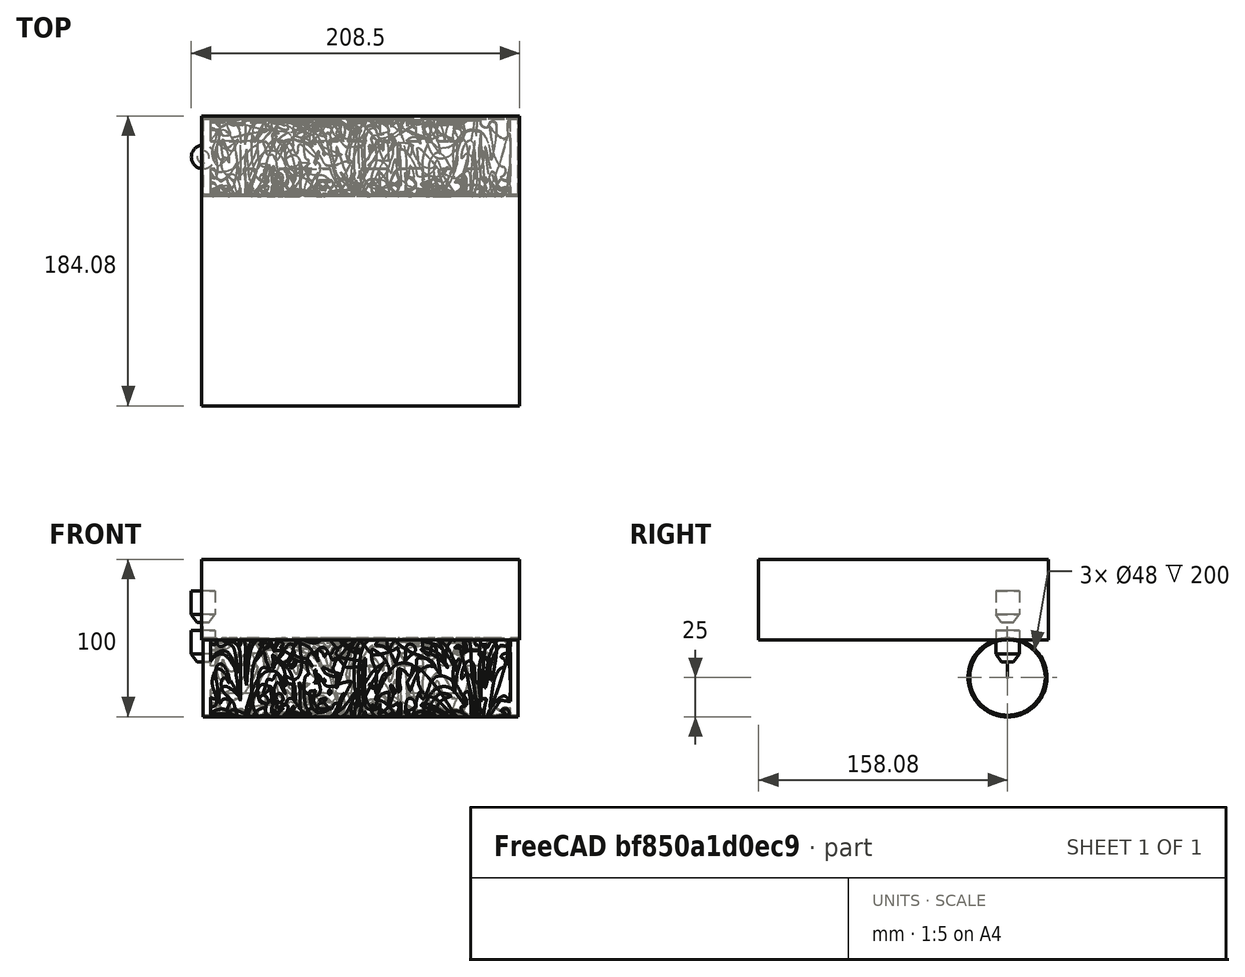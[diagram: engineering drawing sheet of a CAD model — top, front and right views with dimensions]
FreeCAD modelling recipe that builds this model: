
FCSTD DOCUMENT  (FreeCAD 0.20R25747 (Git))
Label: bamboo1
License: All rights reserved
LicenseURL: http://en.wikipedia.org/wiki/All_rights_reserved
objects: Part::FeaturePython×6, Path::FeaturePython×4, Sketcher::SketchObject×2, Part::Feature×2, App::DocumentObjectGroup×2, PartDesign::Pad×1, PartDesign::Body×1, Part::Cut×1, App::Link×1, App::FeaturePython×1, Path::FeatureCompoundPython×1
note: 14 computed .brp shape members not serialized (recipe doc carries the construction recipe); baked Part::Feature solids carry a one-line shape summary decoded from their .brp

FEATURE [Sketcher::SketchObject] Sketch
  FullyConstrained = true
  MapMode = 5
  Placement = pos=(0,0,0) rot=(0.57735,0.57735,0.57735;2.0944rad)
  Support = -> [YZ_Plane]
  sketch-geometry (2):
    g0: Circle CenterX=0 CenterY=0 CenterZ=0 NormalX=0 NormalY=0 NormalZ=1 AngleXU=0 Radius=25
    g1: Circle CenterX=0 CenterY=0 CenterZ=0 NormalX=0 NormalY=0 NormalZ=1 AngleXU=0 Radius=24
  constraints (4):
    c: Coincident(g0,g-1)
    c: Coincident(g1,g0)
    c: Diameter(g0) = 50
    c: Diameter(g1) = 48
FEATURE [PartDesign::Pad] Pad
  Direction = (1,-2e-16,3e-16)
  Length = 200
  Length2 = 100
  Placement = pos=(0,0,0) rot=(0.57735,0.57735,0.57735;2.0944rad)
  Profile = -> Sketch
  Type = 0
FEATURE [PartDesign::Body] Body
  Group = -> [Sketch,Pad]
  Origin = -> Origin
  Tip = -> Pad
FEATURE [Sketcher::SketchObject] Sketch001
  FullyConstrained = false
  Placement = pos=(100,-2.5e-14,5.5e-14) rot=(0.57735,0.57735,0.57735;2.0944rad)
  Support = -> [Pad]
  sketch-geometry (667):
    g0: BSplineCurve PolesCount=4 KnotsCount=2 Degree=3 IsPeriodic=0
    g1: BSplineCurve PolesCount=2 KnotsCount=2 Degree=1 IsPeriodic=0
    g2: BSplineCurve PolesCount=2 KnotsCount=2 Degree=1 IsPeriodic=0
    g3: BSplineCurve PolesCount=4 KnotsCount=2 Degree=3 IsPeriodic=0
    g4: BSplineCurve PolesCount=4 KnotsCount=2 Degree=3 IsPeriodic=0
    g5: BSplineCurve PolesCount=4 KnotsCount=2 Degree=3 IsPeriodic=0
    g6: BSplineCurve PolesCount=3 KnotsCount=2 Degree=2 IsPeriodic=0
    g7: BSplineCurve PolesCount=4 KnotsCount=2 Degree=3 IsPeriodic=0
    g8: BSplineCurve PolesCount=4 KnotsCount=2 Degree=3 IsPeriodic=0
    g9: BSplineCurve PolesCount=4 KnotsCount=2 Degree=3 IsPeriodic=0
    g10: BSplineCurve PolesCount=2 KnotsCount=2 Degree=1 IsPeriodic=0
    g11: BSplineCurve PolesCount=2 KnotsCount=2 Degree=1 IsPeriodic=0
    g12: BSplineCurve PolesCount=4 KnotsCount=2 Degree=3 IsPeriodic=0
    g13: BSplineCurve PolesCount=4 KnotsCount=2 Degree=3 IsPeriodic=0
    g14: BSplineCurve PolesCount=4 KnotsCount=2 Degree=3 IsPeriodic=0
    g15: BSplineCurve PolesCount=4 KnotsCount=2 Degree=3 IsPeriodic=0
    g16: BSplineCurve PolesCount=4 KnotsCount=2 Degree=3 IsPeriodic=0
    g17: BSplineCurve PolesCount=4 KnotsCount=2 Degree=3 IsPeriodic=0
    g18: BSplineCurve PolesCount=4 KnotsCount=2 Degree=3 IsPeriodic=0
    g19: BSplineCurve PolesCount=4 KnotsCount=2 Degree=3 IsPeriodic=0
    g20: BSplineCurve PolesCount=4 KnotsCount=2 Degree=3 IsPeriodic=0
    g21: BSplineCurve PolesCount=4 KnotsCount=2 Degree=3 IsPeriodic=0
    g22: BSplineCurve PolesCount=4 KnotsCount=2 Degree=3 IsPeriodic=0
    g23: BSplineCurve PolesCount=4 KnotsCount=2 Degree=3 IsPeriodic=0
    g24: BSplineCurve PolesCount=4 KnotsCount=2 Degree=3 IsPeriodic=0
    g25: BSplineCurve PolesCount=4 KnotsCount=2 Degree=3 IsPeriodic=0
    g26: BSplineCurve PolesCount=4 KnotsCount=2 Degree=3 IsPeriodic=0
    g27: BSplineCurve PolesCount=4 KnotsCount=2 Degree=3 IsPeriodic=0
    g28: BSplineCurve PolesCount=4 KnotsCount=2 Degree=3 IsPeriodic=0
    g29: BSplineCurve PolesCount=4 KnotsCount=2 Degree=3 IsPeriodic=0
    g30: BSplineCurve PolesCount=4 KnotsCount=2 Degree=3 IsPeriodic=0
    g31: BSplineCurve PolesCount=4 KnotsCount=2 Degree=3 IsPeriodic=0
    g32: BSplineCurve PolesCount=4 KnotsCount=2 Degree=3 IsPeriodic=0
    g33: BSplineCurve PolesCount=4 KnotsCount=2 Degree=3 IsPeriodic=0
    g34: BSplineCurve PolesCount=2 KnotsCount=2 Degree=1 IsPeriodic=0
    g35: BSplineCurve PolesCount=2 KnotsCount=2 Degree=1 IsPeriodic=0
    g36: BSplineCurve PolesCount=4 KnotsCount=2 Degree=3 IsPeriodic=0
    g37: BSplineCurve PolesCount=4 KnotsCount=2 Degree=3 IsPeriodic=0
    g38: BSplineCurve PolesCount=2 KnotsCount=2 Degree=1 IsPeriodic=0
    g39: BSplineCurve PolesCount=2 KnotsCount=2 Degree=1 IsPeriodic=0
    g40: BSplineCurve PolesCount=4 KnotsCount=2 Degree=3 IsPeriodic=0
    g41: BSplineCurve PolesCount=4 KnotsCount=2 Degree=3 IsPeriodic=0
    g42: BSplineCurve PolesCount=4 KnotsCount=2 Degree=3 IsPeriodic=0
    g43: BSplineCurve PolesCount=4 KnotsCount=2 Degree=3 IsPeriodic=0
    g44: BSplineCurve PolesCount=3 KnotsCount=2 Degree=2 IsPeriodic=0
    g45: BSplineCurve PolesCount=4 KnotsCount=2 Degree=3 IsPeriodic=0
    g46: BSplineCurve PolesCount=4 KnotsCount=2 Degree=3 IsPeriodic=0
    g47: BSplineCurve PolesCount=2 KnotsCount=2 Degree=1 IsPeriodic=0
    g48: BSplineCurve PolesCount=2 KnotsCount=2 Degree=1 IsPeriodic=0
    g49: BSplineCurve PolesCount=4 KnotsCount=2 Degree=3 IsPeriodic=0
    g50: BSplineCurve PolesCount=4 KnotsCount=2 Degree=3 IsPeriodic=0
    g51: BSplineCurve PolesCount=4 KnotsCount=2 Degree=3 IsPeriodic=0
    g52: BSplineCurve PolesCount=4 KnotsCount=2 Degree=3 IsPeriodic=0
    g53: BSplineCurve PolesCount=4 KnotsCount=2 Degree=3 IsPeriodic=0
    g54: BSplineCurve PolesCount=4 KnotsCount=2 Degree=3 IsPeriodic=0
    g55: BSplineCurve PolesCount=4 KnotsCount=2 Degree=3 IsPeriodic=0
    g56: BSplineCurve PolesCount=4 KnotsCount=2 Degree=3 IsPeriodic=0
    g57: BSplineCurve PolesCount=4 KnotsCount=2 Degree=3 IsPeriodic=0
    g58: BSplineCurve PolesCount=4 KnotsCount=2 Degree=3 IsPeriodic=0
    g59: BSplineCurve PolesCount=4 KnotsCount=2 Degree=3 IsPeriodic=0
    g60: BSplineCurve PolesCount=4 KnotsCount=2 Degree=3 IsPeriodic=0
    g61: BSplineCurve PolesCount=4 KnotsCount=2 Degree=3 IsPeriodic=0
    g62: BSplineCurve PolesCount=2 KnotsCount=2 Degree=1 IsPeriodic=0
    g63: BSplineCurve PolesCount=2 KnotsCount=2 Degree=1 IsPeriodic=0
    g64: BSplineCurve PolesCount=4 KnotsCount=2 Degree=3 IsPeriodic=0
    g65: BSplineCurve PolesCount=4 KnotsCount=2 Degree=3 IsPeriodic=0
    g66: BSplineCurve PolesCount=2 KnotsCount=2 Degree=1 IsPeriodic=0
    g67: BSplineCurve PolesCount=4 KnotsCount=2 Degree=3 IsPeriodic=0
    g68: BSplineCurve PolesCount=4 KnotsCount=2 Degree=3 IsPeriodic=0
    g69: BSplineCurve PolesCount=4 KnotsCount=2 Degree=3 IsPeriodic=0
    g70: BSplineCurve PolesCount=4 KnotsCount=2 Degree=3 IsPeriodic=0
    g71: BSplineCurve PolesCount=4 KnotsCount=2 Degree=3 IsPeriodic=0
    g72: BSplineCurve PolesCount=4 KnotsCount=2 Degree=3 IsPeriodic=0
    g73: BSplineCurve PolesCount=4 KnotsCount=2 Degree=3 IsPeriodic=0
    g74: BSplineCurve PolesCount=4 KnotsCount=2 Degree=3 IsPeriodic=0
    g75: BSplineCurve PolesCount=4 KnotsCount=2 Degree=3 IsPeriodic=0
    g76: BSplineCurve PolesCount=4 KnotsCount=2 Degree=3 IsPeriodic=0
    g77: BSplineCurve PolesCount=4 KnotsCount=2 Degree=3 IsPeriodic=0
    g78: BSplineCurve PolesCount=4 KnotsCount=2 Degree=3 IsPeriodic=0
    g79: BSplineCurve PolesCount=4 KnotsCount=2 Degree=3 IsPeriodic=0
    g80: BSplineCurve PolesCount=4 KnotsCount=2 Degree=3 IsPeriodic=0
    g81: BSplineCurve PolesCount=4 KnotsCount=2 Degree=3 IsPeriodic=0
    g82: BSplineCurve PolesCount=4 KnotsCount=2 Degree=3 IsPeriodic=0
    g83: BSplineCurve PolesCount=4 KnotsCount=2 Degree=3 IsPeriodic=0
    g84: BSplineCurve PolesCount=4 KnotsCount=2 Degree=3 IsPeriodic=0
    g85: BSplineCurve PolesCount=4 KnotsCount=2 Degree=3 IsPeriodic=0
    g86: BSplineCurve PolesCount=4 KnotsCount=2 Degree=3 IsPeriodic=0
    g87: BSplineCurve PolesCount=4 KnotsCount=2 Degree=3 IsPeriodic=0
    g88: BSplineCurve PolesCount=2 KnotsCount=2 Degree=1 IsPeriodic=0
    g89: BSplineCurve PolesCount=2 KnotsCount=2 Degree=1 IsPeriodic=0
    g90: BSplineCurve PolesCount=4 KnotsCount=2 Degree=3 IsPeriodic=0
    g91: BSplineCurve PolesCount=4 KnotsCount=2 Degree=3 IsPeriodic=0
    g92: BSplineCurve PolesCount=4 KnotsCount=2 Degree=3 IsPeriodic=0
    g93: BSplineCurve PolesCount=4 KnotsCount=2 Degree=3 IsPeriodic=0
    g94: BSplineCurve PolesCount=4 KnotsCount=2 Degree=3 IsPeriodic=0
    g95: BSplineCurve PolesCount=4 KnotsCount=2 Degree=3 IsPeriodic=0
    g96: BSplineCurve PolesCount=4 KnotsCount=2 Degree=3 IsPeriodic=0
    g97: BSplineCurve PolesCount=4 KnotsCount=2 Degree=3 IsPeriodic=0
    g98: BSplineCurve PolesCount=4 KnotsCount=2 Degree=3 IsPeriodic=0
    g99: BSplineCurve PolesCount=4 KnotsCount=2 Degree=3 IsPeriodic=0
    g100: BSplineCurve PolesCount=4 KnotsCount=2 Degree=3 IsPeriodic=0
    g101: BSplineCurve PolesCount=4 KnotsCount=2 Degree=3 IsPeriodic=0
    g102: BSplineCurve PolesCount=4 KnotsCount=2 Degree=3 IsPeriodic=0
    g103: BSplineCurve PolesCount=2 KnotsCount=2 Degree=1 IsPeriodic=0
    g104: BSplineCurve PolesCount=2 KnotsCount=2 Degree=1 IsPeriodic=0
    g105: BSplineCurve PolesCount=4 KnotsCount=2 Degree=3 IsPeriodic=0
    g106: BSplineCurve PolesCount=2 KnotsCount=2 Degree=1 IsPeriodic=0
    g107: BSplineCurve PolesCount=2 KnotsCount=2 Degree=1 IsPeriodic=0
    g108: BSplineCurve PolesCount=2 KnotsCount=2 Degree=1 IsPeriodic=0
    g109: BSplineCurve PolesCount=2 KnotsCount=2 Degree=1 IsPeriodic=0
    g110: BSplineCurve PolesCount=4 KnotsCount=2 Degree=3 IsPeriodic=0
    g111: BSplineCurve PolesCount=4 KnotsCount=2 Degree=3 IsPeriodic=0
    g112: BSplineCurve PolesCount=4 KnotsCount=2 Degree=3 IsPeriodic=0
    g113: BSplineCurve PolesCount=4 KnotsCount=2 Degree=3 IsPeriodic=0
    g114: BSplineCurve PolesCount=4 KnotsCount=2 Degree=3 IsPeriodic=0
    g115: BSplineCurve PolesCount=4 KnotsCount=2 Degree=3 IsPeriodic=0
    g116: BSplineCurve PolesCount=4 KnotsCount=2 Degree=3 IsPeriodic=0
    g117: BSplineCurve PolesCount=4 KnotsCount=2 Degree=3 IsPeriodic=0
    g118: BSplineCurve PolesCount=4 KnotsCount=2 Degree=3 IsPeriodic=0
    g119: BSplineCurve PolesCount=4 KnotsCount=2 Degree=3 IsPeriodic=0
    g120: BSplineCurve PolesCount=4 KnotsCount=2 Degree=3 IsPeriodic=0
    g121: BSplineCurve PolesCount=4 KnotsCount=2 Degree=3 IsPeriodic=0
    g122: BSplineCurve PolesCount=4 KnotsCount=2 Degree=3 IsPeriodic=0
    g123: BSplineCurve PolesCount=4 KnotsCount=2 Degree=3 IsPeriodic=0
    g124: BSplineCurve PolesCount=4 KnotsCount=2 Degree=3 IsPeriodic=0
    g125: BSplineCurve PolesCount=4 KnotsCount=2 Degree=3 IsPeriodic=0
    g126: BSplineCurve PolesCount=4 KnotsCount=2 Degree=3 IsPeriodic=0
    g127: BSplineCurve PolesCount=4 KnotsCount=2 Degree=3 IsPeriodic=0
    g128: BSplineCurve PolesCount=4 KnotsCount=2 Degree=3 IsPeriodic=0
    g129: BSplineCurve PolesCount=4 KnotsCount=2 Degree=3 IsPeriodic=0
    g130: BSplineCurve PolesCount=4 KnotsCount=2 Degree=3 IsPeriodic=0
    g131: BSplineCurve PolesCount=4 KnotsCount=2 Degree=3 IsPeriodic=0
    g132: BSplineCurve PolesCount=4 KnotsCount=2 Degree=3 IsPeriodic=0
    g133: BSplineCurve PolesCount=4 KnotsCount=2 Degree=3 IsPeriodic=0
    g134: BSplineCurve PolesCount=4 KnotsCount=2 Degree=3 IsPeriodic=0
    g135: BSplineCurve PolesCount=4 KnotsCount=2 Degree=3 IsPeriodic=0
    g136: BSplineCurve PolesCount=4 KnotsCount=2 Degree=3 IsPeriodic=0
    g137: BSplineCurve PolesCount=4 KnotsCount=2 Degree=3 IsPeriodic=0
    g138: BSplineCurve PolesCount=4 KnotsCount=2 Degree=3 IsPeriodic=0
    g139: BSplineCurve PolesCount=3 KnotsCount=2 Degree=2 IsPeriodic=0
    g140: BSplineCurve PolesCount=4 KnotsCount=2 Degree=3 IsPeriodic=0
    g141: BSplineCurve PolesCount=4 KnotsCount=2 Degree=3 IsPeriodic=0
    g142: BSplineCurve PolesCount=4 KnotsCount=2 Degree=3 IsPeriodic=0
    g143: BSplineCurve PolesCount=4 KnotsCount=2 Degree=3 IsPeriodic=0
    g144: BSplineCurve PolesCount=4 KnotsCount=2 Degree=3 IsPeriodic=0
    g145: BSplineCurve PolesCount=2 KnotsCount=2 Degree=1 IsPeriodic=0
    g146: BSplineCurve PolesCount=2 KnotsCount=2 Degree=1 IsPeriodic=0
    g147: BSplineCurve PolesCount=4 KnotsCount=2 Degree=3 IsPeriodic=0
    g148: BSplineCurve PolesCount=4 KnotsCount=2 Degree=3 IsPeriodic=0
    g149: BSplineCurve PolesCount=4 KnotsCount=2 Degree=3 IsPeriodic=0
    g150: BSplineCurve PolesCount=4 KnotsCount=2 Degree=3 IsPeriodic=0
    g151: BSplineCurve PolesCount=4 KnotsCount=2 Degree=3 IsPeriodic=0
    g152: BSplineCurve PolesCount=4 KnotsCount=2 Degree=3 IsPeriodic=0
    g153: BSplineCurve PolesCount=4 KnotsCount=2 Degree=3 IsPeriodic=0
    g154: BSplineCurve PolesCount=4 KnotsCount=2 Degree=3 IsPeriodic=0
    g155: BSplineCurve PolesCount=4 KnotsCount=2 Degree=3 IsPeriodic=0
    g156: BSplineCurve PolesCount=4 KnotsCount=2 Degree=3 IsPeriodic=0
    g157: BSplineCurve PolesCount=4 KnotsCount=2 Degree=3 IsPeriodic=0
    g158: BSplineCurve PolesCount=4 KnotsCount=2 Degree=3 IsPeriodic=0
    g159: BSplineCurve PolesCount=2 KnotsCount=2 Degree=1 IsPeriodic=0
    g160: BSplineCurve PolesCount=2 KnotsCount=2 Degree=1 IsPeriodic=0
    g161: BSplineCurve PolesCount=4 KnotsCount=2 Degree=3 IsPeriodic=0
    g162: BSplineCurve PolesCount=4 KnotsCount=2 Degree=3 IsPeriodic=0
    g163: BSplineCurve PolesCount=4 KnotsCount=2 Degree=3 IsPeriodic=0
    g164: BSplineCurve PolesCount=4 KnotsCount=2 Degree=3 IsPeriodic=0
    g165: BSplineCurve PolesCount=4 KnotsCount=2 Degree=3 IsPeriodic=0
    g166: BSplineCurve PolesCount=4 KnotsCount=2 Degree=3 IsPeriodic=0
    g167: BSplineCurve PolesCount=4 KnotsCount=2 Degree=3 IsPeriodic=0
    g168: BSplineCurve PolesCount=4 KnotsCount=2 Degree=3 IsPeriodic=0
    g169: BSplineCurve PolesCount=4 KnotsCount=2 Degree=3 IsPeriodic=0
    g170: BSplineCurve PolesCount=2 KnotsCount=2 Degree=1 IsPeriodic=0
    g171: BSplineCurve PolesCount=2 KnotsCount=2 Degree=1 IsPeriodic=0
    g172: BSplineCurve PolesCount=4 KnotsCount=2 Degree=3 IsPeriodic=0
    g173: BSplineCurve PolesCount=4 KnotsCount=2 Degree=3 IsPeriodic=0
    g174: BSplineCurve PolesCount=4 KnotsCount=2 Degree=3 IsPeriodic=0
    g175: BSplineCurve PolesCount=3 KnotsCount=2 Degree=2 IsPeriodic=0
    g176: BSplineCurve PolesCount=4 KnotsCount=2 Degree=3 IsPeriodic=0
    g177: BSplineCurve PolesCount=4 KnotsCount=2 Degree=3 IsPeriodic=0
    g178: BSplineCurve PolesCount=4 KnotsCount=2 Degree=3 IsPeriodic=0
    g179: BSplineCurve PolesCount=4 KnotsCount=2 Degree=3 IsPeriodic=0
    g180: BSplineCurve PolesCount=3 KnotsCount=2 Degree=2 IsPeriodic=0
    g181: BSplineCurve PolesCount=2 KnotsCount=2 Degree=1 IsPeriodic=0
    g182: BSplineCurve PolesCount=2 KnotsCount=2 Degree=1 IsPeriodic=0
    g183: BSplineCurve PolesCount=4 KnotsCount=2 Degree=3 IsPeriodic=0
    g184: BSplineCurve PolesCount=4 KnotsCount=2 Degree=3 IsPeriodic=0
    g185: BSplineCurve PolesCount=2 KnotsCount=2 Degree=1 IsPeriodic=0
    g186: BSplineCurve PolesCount=2 KnotsCount=2 Degree=1 IsPeriodic=0
    g187: BSplineCurve PolesCount=3 KnotsCount=2 Degree=2 IsPeriodic=0
    g188: BSplineCurve PolesCount=4 KnotsCount=2 Degree=3 IsPeriodic=0
    g189: BSplineCurve PolesCount=4 KnotsCount=2 Degree=3 IsPeriodic=0
    g190: BSplineCurve PolesCount=4 KnotsCount=2 Degree=3 IsPeriodic=0
    g191: BSplineCurve PolesCount=4 KnotsCount=2 Degree=3 IsPeriodic=0
    g192: BSplineCurve PolesCount=4 KnotsCount=2 Degree=3 IsPeriodic=0
    g193: BSplineCurve PolesCount=4 KnotsCount=2 Degree=3 IsPeriodic=0
    g194: BSplineCurve PolesCount=4 KnotsCount=2 Degree=3 IsPeriodic=0
    g195: BSplineCurve PolesCount=4 KnotsCount=2 Degree=3 IsPeriodic=0
    g196: BSplineCurve PolesCount=4 KnotsCount=2 Degree=3 IsPeriodic=0
    g197: BSplineCurve PolesCount=4 KnotsCount=2 Degree=3 IsPeriodic=0
    g198: BSplineCurve PolesCount=4 KnotsCount=2 Degree=3 IsPeriodic=0
    g199: BSplineCurve PolesCount=4 KnotsCount=2 Degree=3 IsPeriodic=0
    g200: BSplineCurve PolesCount=4 KnotsCount=2 Degree=3 IsPeriodic=0
    g201: BSplineCurve PolesCount=4 KnotsCount=2 Degree=3 IsPeriodic=0
    g202: BSplineCurve PolesCount=4 KnotsCount=2 Degree=3 IsPeriodic=0
    g203: BSplineCurve PolesCount=4 KnotsCount=2 Degree=3 IsPeriodic=0
    g204: BSplineCurve PolesCount=3 KnotsCount=2 Degree=2 IsPeriodic=0
    g205: BSplineCurve PolesCount=4 KnotsCount=2 Degree=3 IsPeriodic=0
    g206: BSplineCurve PolesCount=2 KnotsCount=2 Degree=1 IsPeriodic=0
    g207: BSplineCurve PolesCount=2 KnotsCount=2 Degree=1 IsPeriodic=0
    g208: BSplineCurve PolesCount=4 KnotsCount=2 Degree=3 IsPeriodic=0
    g209: BSplineCurve PolesCount=4 KnotsCount=2 Degree=3 IsPeriodic=0
    g210: BSplineCurve PolesCount=4 KnotsCount=2 Degree=3 IsPeriodic=0
    g211: BSplineCurve PolesCount=4 KnotsCount=2 Degree=3 IsPeriodic=0
    g212: BSplineCurve PolesCount=4 KnotsCount=2 Degree=3 IsPeriodic=0
    g213: BSplineCurve PolesCount=3 KnotsCount=2 Degree=2 IsPeriodic=0
    g214: BSplineCurve PolesCount=2 KnotsCount=2 Degree=1 IsPeriodic=0
    g215: BSplineCurve PolesCount=4 KnotsCount=2 Degree=3 IsPeriodic=0
    g216: BSplineCurve PolesCount=2 KnotsCount=2 Degree=1 IsPeriodic=0
    g217: BSplineCurve PolesCount=2 KnotsCount=2 Degree=1 IsPeriodic=0
    g218: BSplineCurve PolesCount=4 KnotsCount=2 Degree=3 IsPeriodic=0
    g219: BSplineCurve PolesCount=4 KnotsCount=2 Degree=3 IsPeriodic=0
    g220: BSplineCurve PolesCount=4 KnotsCount=2 Degree=3 IsPeriodic=0
    g221: BSplineCurve PolesCount=4 KnotsCount=2 Degree=3 IsPeriodic=0
    g222: BSplineCurve PolesCount=4 KnotsCount=2 Degree=3 IsPeriodic=0
    g223: BSplineCurve PolesCount=4 KnotsCount=2 Degree=3 IsPeriodic=0
    g224: BSplineCurve PolesCount=4 KnotsCount=2 Degree=3 IsPeriodic=0
    g225: BSplineCurve PolesCount=4 KnotsCount=2 Degree=3 IsPeriodic=0
    g226: BSplineCurve PolesCount=4 KnotsCount=2 Degree=3 IsPeriodic=0
    g227: BSplineCurve PolesCount=2 KnotsCount=2 Degree=1 IsPeriodic=0
    g228: BSplineCurve PolesCount=2 KnotsCount=2 Degree=1 IsPeriodic=0
    g229: BSplineCurve PolesCount=4 KnotsCount=2 Degree=3 IsPeriodic=0
    g230: BSplineCurve PolesCount=4 KnotsCount=2 Degree=3 IsPeriodic=0
    g231: BSplineCurve PolesCount=4 KnotsCount=2 Degree=3 IsPeriodic=0
    g232: BSplineCurve PolesCount=4 KnotsCount=2 Degree=3 IsPeriodic=0
    g233: BSplineCurve PolesCount=4 KnotsCount=2 Degree=3 IsPeriodic=0
    g234: BSplineCurve PolesCount=4 KnotsCount=2 Degree=3 IsPeriodic=0
    g235: BSplineCurve PolesCount=4 KnotsCount=2 Degree=3 IsPeriodic=0
    g236: BSplineCurve PolesCount=4 KnotsCount=2 Degree=3 IsPeriodic=0
    g237: BSplineCurve PolesCount=4 KnotsCount=2 Degree=3 IsPeriodic=0
    g238: BSplineCurve PolesCount=4 KnotsCount=2 Degree=3 IsPeriodic=0
    g239: BSplineCurve PolesCount=4 KnotsCount=2 Degree=3 IsPeriodic=0
    g240: BSplineCurve PolesCount=2 KnotsCount=2 Degree=1 IsPeriodic=0
    g241: BSplineCurve PolesCount=2 KnotsCount=2 Degree=1 IsPeriodic=0
    g242: BSplineCurve PolesCount=4 KnotsCount=2 Degree=3 IsPeriodic=0
    g243: BSplineCurve PolesCount=4 KnotsCount=2 Degree=3 IsPeriodic=0
    g244: BSplineCurve PolesCount=4 KnotsCount=2 Degree=3 IsPeriodic=0
    g245: BSplineCurve PolesCount=4 KnotsCount=2 Degree=3 IsPeriodic=0
    g246: BSplineCurve PolesCount=4 KnotsCount=2 Degree=3 IsPeriodic=0
    g247: BSplineCurve PolesCount=4 KnotsCount=2 Degree=3 IsPeriodic=0
    g248: BSplineCurve PolesCount=4 KnotsCount=2 Degree=3 IsPeriodic=0
    g249: BSplineCurve PolesCount=4 KnotsCount=2 Degree=3 IsPeriodic=0
    g250: BSplineCurve PolesCount=4 KnotsCount=2 Degree=3 IsPeriodic=0
    g251: BSplineCurve PolesCount=2 KnotsCount=2 Degree=1 IsPeriodic=0
    g252: BSplineCurve PolesCount=4 KnotsCount=2 Degree=3 IsPeriodic=0
    g253: BSplineCurve PolesCount=4 KnotsCount=2 Degree=3 IsPeriodic=0
    g254: BSplineCurve PolesCount=4 KnotsCount=2 Degree=3 IsPeriodic=0
    g255: BSplineCurve PolesCount=4 KnotsCount=2 Degree=3 IsPeriodic=0
    g256: BSplineCurve PolesCount=4 KnotsCount=2 Degree=3 IsPeriodic=0
    g257: BSplineCurve PolesCount=4 KnotsCount=2 Degree=3 IsPeriodic=0
    g258: BSplineCurve PolesCount=4 KnotsCount=2 Degree=3 IsPeriodic=0
    g259: BSplineCurve PolesCount=4 KnotsCount=2 Degree=3 IsPeriodic=0
    g260: BSplineCurve PolesCount=4 KnotsCount=2 Degree=3 IsPeriodic=0
    g261: BSplineCurve PolesCount=4 KnotsCount=2 Degree=3 IsPeriodic=0
    g262: BSplineCurve PolesCount=4 KnotsCount=2 Degree=3 IsPeriodic=0
    g263: BSplineCurve PolesCount=4 KnotsCount=2 Degree=3 IsPeriodic=0
    g264: BSplineCurve PolesCount=4 KnotsCount=2 Degree=3 IsPeriodic=0
    g265: BSplineCurve PolesCount=4 KnotsCount=2 Degree=3 IsPeriodic=0
    g266: BSplineCurve PolesCount=4 KnotsCount=2 Degree=3 IsPeriodic=0
    g267: BSplineCurve PolesCount=4 KnotsCount=2 Degree=3 IsPeriodic=0
    g268: BSplineCurve PolesCount=4 KnotsCount=2 Degree=3 IsPeriodic=0
    g269: BSplineCurve PolesCount=4 KnotsCount=2 Degree=3 IsPeriodic=0
    g270: BSplineCurve PolesCount=4 KnotsCount=2 Degree=3 IsPeriodic=0
    g271: BSplineCurve PolesCount=4 KnotsCount=2 Degree=3 IsPeriodic=0
    g272: BSplineCurve PolesCount=4 KnotsCount=2 Degree=3 IsPeriodic=0
    g273: BSplineCurve PolesCount=4 KnotsCount=2 Degree=3 IsPeriodic=0
    g274: BSplineCurve PolesCount=4 KnotsCount=2 Degree=3 IsPeriodic=0
    g275: BSplineCurve PolesCount=2 KnotsCount=2 Degree=1 IsPeriodic=0
    g276: BSplineCurve PolesCount=2 KnotsCount=2 Degree=1 IsPeriodic=0
    g277: BSplineCurve PolesCount=4 KnotsCount=2 Degree=3 IsPeriodic=0
    g278: BSplineCurve PolesCount=4 KnotsCount=2 Degree=3 IsPeriodic=0
    g279: BSplineCurve PolesCount=2 KnotsCount=2 Degree=1 IsPeriodic=0
    g280: BSplineCurve PolesCount=4 KnotsCount=2 Degree=3 IsPeriodic=0
    g281: BSplineCurve PolesCount=4 KnotsCount=2 Degree=3 IsPeriodic=0
    g282: BSplineCurve PolesCount=4 KnotsCount=2 Degree=3 IsPeriodic=0
    g283: BSplineCurve PolesCount=4 KnotsCount=2 Degree=3 IsPeriodic=0
    g284: BSplineCurve PolesCount=2 KnotsCount=2 Degree=1 IsPeriodic=0
    g285: BSplineCurve PolesCount=2 KnotsCount=2 Degree=1 IsPeriodic=0
    g286: BSplineCurve PolesCount=4 KnotsCount=2 Degree=3 IsPeriodic=0
    g287: BSplineCurve PolesCount=4 KnotsCount=2 Degree=3 IsPeriodic=0
    g288: BSplineCurve PolesCount=4 KnotsCount=2 Degree=3 IsPeriodic=0
    g289: BSplineCurve PolesCount=4 KnotsCount=2 Degree=3 IsPeriodic=0
    g290: BSplineCurve PolesCount=4 KnotsCount=2 Degree=3 IsPeriodic=0
    g291: BSplineCurve PolesCount=4 KnotsCount=2 Degree=3 IsPeriodic=0
    g292: BSplineCurve PolesCount=4 KnotsCount=2 Degree=3 IsPeriodic=0
    g293: BSplineCurve PolesCount=4 KnotsCount=2 Degree=3 IsPeriodic=0
    g294: BSplineCurve PolesCount=2 KnotsCount=2 Degree=1 IsPeriodic=0
    g295: BSplineCurve PolesCount=2 KnotsCount=2 Degree=1 IsPeriodic=0
    g296: BSplineCurve PolesCount=3 KnotsCount=2 Degree=2 IsPeriodic=0
    g297: BSplineCurve PolesCount=4 KnotsCount=2 Degree=3 IsPeriodic=0
    g298: BSplineCurve PolesCount=4 KnotsCount=2 Degree=3 IsPeriodic=0
    g299: BSplineCurve PolesCount=4 KnotsCount=2 Degree=3 IsPeriodic=0
    g300: BSplineCurve PolesCount=3 KnotsCount=2 Degree=2 IsPeriodic=0
    g301: BSplineCurve PolesCount=2 KnotsCount=2 Degree=1 IsPeriodic=0
    g302: BSplineCurve PolesCount=2 KnotsCount=2 Degree=1 IsPeriodic=0
    g303: BSplineCurve PolesCount=4 KnotsCount=2 Degree=3 IsPeriodic=0
    g304: BSplineCurve PolesCount=4 KnotsCount=2 Degree=3 IsPeriodic=0
    g305: BSplineCurve PolesCount=2 KnotsCount=2 Degree=1 IsPeriodic=0
    g306: BSplineCurve PolesCount=2 KnotsCount=2 Degree=1 IsPeriodic=0
    g307: BSplineCurve PolesCount=2 KnotsCount=2 Degree=1 IsPeriodic=0
    g308: BSplineCurve PolesCount=2 KnotsCount=2 Degree=1 IsPeriodic=0
    g309: BSplineCurve PolesCount=4 KnotsCount=2 Degree=3 IsPeriodic=0
    g310: BSplineCurve PolesCount=2 KnotsCount=2 Degree=1 IsPeriodic=0
    g311: BSplineCurve PolesCount=2 KnotsCount=2 Degree=1 IsPeriodic=0
    g312: BSplineCurve PolesCount=4 KnotsCount=2 Degree=3 IsPeriodic=0
    g313: BSplineCurve PolesCount=4 KnotsCount=2 Degree=3 IsPeriodic=0
    g314: BSplineCurve PolesCount=4 KnotsCount=2 Degree=3 IsPeriodic=0
    g315: BSplineCurve PolesCount=4 KnotsCount=2 Degree=3 IsPeriodic=0
    g316: BSplineCurve PolesCount=4 KnotsCount=2 Degree=3 IsPeriodic=0
    g317: BSplineCurve PolesCount=4 KnotsCount=2 Degree=3 IsPeriodic=0
    g318: BSplineCurve PolesCount=4 KnotsCount=2 Degree=3 IsPeriodic=0
    g319: BSplineCurve PolesCount=4 KnotsCount=2 Degree=3 IsPeriodic=0
    g320: BSplineCurve PolesCount=4 KnotsCount=2 Degree=3 IsPeriodic=0
    g321: BSplineCurve PolesCount=4 KnotsCount=2 Degree=3 IsPeriodic=0
    g322: BSplineCurve PolesCount=4 KnotsCount=2 Degree=3 IsPeriodic=0
    g323: BSplineCurve PolesCount=4 KnotsCount=2 Degree=3 IsPeriodic=0
    g324: BSplineCurve PolesCount=4 KnotsCount=2 Degree=3 IsPeriodic=0
    g325: BSplineCurve PolesCount=4 KnotsCount=2 Degree=3 IsPeriodic=0
    g326: BSplineCurve PolesCount=4 KnotsCount=2 Degree=3 IsPeriodic=0
    g327: BSplineCurve PolesCount=4 KnotsCount=2 Degree=3 IsPeriodic=0
    g328: BSplineCurve PolesCount=4 KnotsCount=2 Degree=3 IsPeriodic=0
    g329: BSplineCurve PolesCount=4 KnotsCount=2 Degree=3 IsPeriodic=0
    g330: BSplineCurve PolesCount=4 KnotsCount=2 Degree=3 IsPeriodic=0
    g331: BSplineCurve PolesCount=2 KnotsCount=2 Degree=1 IsPeriodic=0
    g332: BSplineCurve PolesCount=2 KnotsCount=2 Degree=1 IsPeriodic=0
    g333: BSplineCurve PolesCount=4 KnotsCount=2 Degree=3 IsPeriodic=0
    g334: BSplineCurve PolesCount=4 KnotsCount=2 Degree=3 IsPeriodic=0
    g335: BSplineCurve PolesCount=4 KnotsCount=2 Degree=3 IsPeriodic=0
    g336: BSplineCurve PolesCount=2 KnotsCount=2 Degree=1 IsPeriodic=0
    g337: BSplineCurve PolesCount=2 KnotsCount=2 Degree=1 IsPeriodic=0
    g338: BSplineCurve PolesCount=4 KnotsCount=2 Degree=3 IsPeriodic=0
    g339: BSplineCurve PolesCount=2 KnotsCount=2 Degree=1 IsPeriodic=0
    g340: BSplineCurve PolesCount=2 KnotsCount=2 Degree=1 IsPeriodic=0
    g341: BSplineCurve PolesCount=2 KnotsCount=2 Degree=1 IsPeriodic=0
    g342: BSplineCurve PolesCount=2 KnotsCount=2 Degree=1 IsPeriodic=0
    g343: BSplineCurve PolesCount=4 KnotsCount=2 Degree=3 IsPeriodic=0
    g344: BSplineCurve PolesCount=4 KnotsCount=2 Degree=3 IsPeriodic=0
    g345: BSplineCurve PolesCount=4 KnotsCount=2 Degree=3 IsPeriodic=0
    g346: BSplineCurve PolesCount=4 KnotsCount=2 Degree=3 IsPeriodic=0
    g347: BSplineCurve PolesCount=4 KnotsCount=2 Degree=3 IsPeriodic=0
    g348: BSplineCurve PolesCount=2 KnotsCount=2 Degree=1 IsPeriodic=0
    g349: BSplineCurve PolesCount=2 KnotsCount=2 Degree=1 IsPeriodic=0
    g350: BSplineCurve PolesCount=4 KnotsCount=2 Degree=3 IsPeriodic=0
    g351: BSplineCurve PolesCount=4 KnotsCount=2 Degree=3 IsPeriodic=0
    g352: BSplineCurve PolesCount=4 KnotsCount=2 Degree=3 IsPeriodic=0
    g353: BSplineCurve PolesCount=4 KnotsCount=2 Degree=3 IsPeriodic=0
    g354: BSplineCurve PolesCount=4 KnotsCount=2 Degree=3 IsPeriodic=0
    g355: BSplineCurve PolesCount=4 KnotsCount=2 Degree=3 IsPeriodic=0
    g356: BSplineCurve PolesCount=4 KnotsCount=2 Degree=3 IsPeriodic=0
    g357: BSplineCurve PolesCount=4 KnotsCount=2 Degree=3 IsPeriodic=0
    g358: BSplineCurve PolesCount=4 KnotsCount=2 Degree=3 IsPeriodic=0
    g359: BSplineCurve PolesCount=4 KnotsCount=2 Degree=3 IsPeriodic=0
    g360: BSplineCurve PolesCount=4 KnotsCount=2 Degree=3 IsPeriodic=0
    g361: BSplineCurve PolesCount=4 KnotsCount=2 Degree=3 IsPeriodic=0
    g362: BSplineCurve PolesCount=4 KnotsCount=2 Degree=3 IsPeriodic=0
    g363: BSplineCurve PolesCount=4 KnotsCount=2 Degree=3 IsPeriodic=0
    g364: BSplineCurve PolesCount=4 KnotsCount=2 Degree=3 IsPeriodic=0
    g365: BSplineCurve PolesCount=4 KnotsCount=2 Degree=3 IsPeriodic=0
    g366: BSplineCurve PolesCount=4 KnotsCount=2 Degree=3 IsPeriodic=0
    g367: BSplineCurve PolesCount=4 KnotsCount=2 Degree=3 IsPeriodic=0
    g368: BSplineCurve PolesCount=4 KnotsCount=2 Degree=3 IsPeriodic=0
    g369: BSplineCurve PolesCount=4 KnotsCount=2 Degree=3 IsPeriodic=0
    g370: BSplineCurve PolesCount=4 KnotsCount=2 Degree=3 IsPeriodic=0
    g371: BSplineCurve PolesCount=4 KnotsCount=2 Degree=3 IsPeriodic=0
    g372: BSplineCurve PolesCount=2 KnotsCount=2 Degree=1 IsPeriodic=0
    g373: BSplineCurve PolesCount=2 KnotsCount=2 Degree=1 IsPeriodic=0
    g374: BSplineCurve PolesCount=4 KnotsCount=2 Degree=3 IsPeriodic=0
    g375: BSplineCurve PolesCount=4 KnotsCount=2 Degree=3 IsPeriodic=0
    g376: BSplineCurve PolesCount=4 KnotsCount=2 Degree=3 IsPeriodic=0
    g377: BSplineCurve PolesCount=4 KnotsCount=2 Degree=3 IsPeriodic=0
    g378: BSplineCurve PolesCount=4 KnotsCount=2 Degree=3 IsPeriodic=0
    g379: BSplineCurve PolesCount=4 KnotsCount=2 Degree=3 IsPeriodic=0
    g380: BSplineCurve PolesCount=4 KnotsCount=2 Degree=3 IsPeriodic=0
    g381: BSplineCurve PolesCount=4 KnotsCount=2 Degree=3 IsPeriodic=0
    g382: BSplineCurve PolesCount=4 KnotsCount=2 Degree=3 IsPeriodic=0
    g383: BSplineCurve PolesCount=4 KnotsCount=2 Degree=3 IsPeriodic=0
    g384: BSplineCurve PolesCount=4 KnotsCount=2 Degree=3 IsPeriodic=0
    g385: BSplineCurve PolesCount=4 KnotsCount=2 Degree=3 IsPeriodic=0
    g386: BSplineCurve PolesCount=4 KnotsCount=2 Degree=3 IsPeriodic=0
    g387: BSplineCurve PolesCount=4 KnotsCount=2 Degree=3 IsPeriodic=0
    g388: BSplineCurve PolesCount=4 KnotsCount=2 Degree=3 IsPeriodic=0
    g389: BSplineCurve PolesCount=2 KnotsCount=2 Degree=1 IsPeriodic=0
    g390: BSplineCurve PolesCount=2 KnotsCount=2 Degree=1 IsPeriodic=0
    g391: BSplineCurve PolesCount=4 KnotsCount=2 Degree=3 IsPeriodic=0
    g392: BSplineCurve PolesCount=4 KnotsCount=2 Degree=3 IsPeriodic=0
    g393: BSplineCurve PolesCount=4 KnotsCount=2 Degree=3 IsPeriodic=0
    g394: BSplineCurve PolesCount=2 KnotsCount=2 Degree=1 IsPeriodic=0
    g395: BSplineCurve PolesCount=2 KnotsCount=2 Degree=1 IsPeriodic=0
    g396: BSplineCurve PolesCount=4 KnotsCount=2 Degree=3 IsPeriodic=0
    g397: BSplineCurve PolesCount=4 KnotsCount=2 Degree=3 IsPeriodic=0
    g398: BSplineCurve PolesCount=4 KnotsCount=2 Degree=3 IsPeriodic=0
    g399: BSplineCurve PolesCount=4 KnotsCount=2 Degree=3 IsPeriodic=0
    ... +267 more geometry lines
  constraints (8):
    c: Coincident(g663,g664)
    c: Coincident(g664,g665)
    c: Coincident(g665,g666)
    c: Coincident(g666,g663)
    c: Horizontal(g663)
    c: Horizontal(g665)
    c: Vertical(g664)
    c: Vertical(g666)
FEATURE [Part::FeaturePython] Sketch_On_Surface  # WARN: FeaturePython — macro-defined, semantics opaque (R4)
  ConstructionBounds = true
  FillExtrusion = true
  FillFaces = true
  ReverseU = false
  ReverseV = false
  Sketch = -> Sketch001
  SwapUV = false
  Thickness = -3
FEATURE [Part::Cut] Cut
  Base = -> Pad
  Tool = -> Sketch_On_Surface
FEATURE [Part::Feature] Cut001
  Placement = pos=(0,0,0) rot=(1,0,0;1.5708rad)
  shape: bbox 200 x 50.88 x 50.52 mm, 667 faces (baked)
FEATURE [Part::Feature] Shape
  shape: bbox 200 x 157.1 x 2e-07 mm, 0 faces, 0 solids (baked)
FEATURE [App::Link] Link  label="Cut002"
  LinkTransform = true
  LinkedObject = -> Cut001
FEATURE [App::FeaturePython] SetupSheet  # Path/CAM operation (typed FeaturePython)
  ClearanceHeightExpression = OpStockZMax+SetupSheet.ClearanceHeightOffset
  ClearanceHeightOffset = 5
  CoolantMode = 0
  CoolantModes = None | Flood | Mist
  FinalDepthExpression = OpFinalDepth
  HorizRapid = 60000
  SafeHeightExpression = OpStockZMax+SetupSheet.SafeHeightOffset
  SafeHeightOffset = 3
  StartDepthExpression = OpStartDepth
  StepDownExpression = OpToolDiameter
  VertRapid = 60000
FEATURE [Part::FeaturePython] Clone  label="Model-Shape"  # Draft clone (typed FeaturePython)
  AttacherType = Attacher::AttachEngine3D
  Fuse = false
  Objects = -> [Shape]
  PathResource = Model
  Scale = (1,1,1)
FEATURE [App::DocumentObjectGroup] Model
  Group = -> [Clone,Link]
FEATURE [Part::FeaturePython] ToolBit  label="100um laser003"  # Path/CAM toolbit (typed FeaturePython)
  BitPropertyNames = Chipload | CuttingEdgeHeight | Diameter | Flutes | Length | Material | ShankDiameter
  BitShape = <userpath>/Documents/GitHub/FreeCADBuild/Mod\Path\Tools\Shape\laser.fcstd
  Chipload = 0
  CuttingEdgeHeight = 10
  Diameter = 0.1
  Flutes = 0
  Length = 30
  Material = 0
  ShankDiameter = 15
  ShapeName = laser
FEATURE [Path::FeaturePython] _00um_laser  label="100um laser001"  # Path/CAM operation (typed FeaturePython)
  HorizFeed = 10000
  HorizRapid = 60000
  SpindleDir = 0
  SpindleSpeed = 0
  Tool = -> ToolBit
  ToolNumber = 2
  VertFeed = 10000
  VertRapid = 60000
  expr: HorizRapid = SetupSheet.HorizRapid
  expr: VertRapid = SetupSheet.VertRapid
FEATURE [App::DocumentObjectGroup] Tools
  Group = -> [_00um_laser]
FEATURE [Part::FeaturePython] Stock  # WARN: FeaturePython — macro-defined, semantics opaque (R4)
  Base = -> Model
  ExtXneg = 1
  ExtXpos = 1
  ExtYneg = 1
  ExtYpos = 1
  ExtZneg = 1
  ExtZpos = 0
  Placement = pos=(-6.4e-14,-157.08,25) rot=(0,0,1;0rad)
  StockType = FromBase
FEATURE [Path::FeaturePython] Engrave  # Path/CAM operation (typed FeaturePython)
  Active = true
  Base = -> [Clone]
  ClearanceHeight = 30
  CoolantMode = None
  CycleTime = 00:00:00
  FinalDepth = 25
  OpFinalDepth = 24.9
  OpStartDepth = 25
  OpStockZMax = 25
  OpStockZMin = 24
  OpToolDiameter = 0.1
  SafeHeight = 28
  StartDepth = 25
  StartVertex = 0
  StepDown = 0
  ToolController = -> _00um_laser
  expr: StepDown = 0
  expr: ClearanceHeight = OpStockZMax + SetupSheet.ClearanceHeightOffset
  expr: SafeHeight = OpStockZMax + SetupSheet.SafeHeightOffset
  expr: StartDepth = OpStartDepth
FEATURE [Path::FeaturePython] AxisMapDressup  # Path/CAM operation (typed FeaturePython)
  AxisMap = 1
  Base = -> Engrave
  Radius = 25
FEATURE [Path::FeatureCompoundPython] Operations  # Path/CAM operation (typed FeaturePython)
  Group = -> [AxisMapDressup]
  UsePlacements = false
FEATURE [Path::FeaturePython] Job  # Path/CAM operation (typed FeaturePython)
  CycleTime = 00:00:00
  Fixtures = G54
  GeometryTolerance = 0.01
  Model = -> Model
  Operations = -> Operations
  OrderOutputBy = 0
  PostProcessor = 7
  SetupSheet = -> SetupSheet
  SplitOutput = false
  Stock = -> Stock
  Tools = -> Tools
FEATURE [Part::FeaturePython] CutTool  # WARN: FeaturePython — macro-defined, semantics opaque (R4)
  Placement = pos=(6e-15,0,25) rot=(0,0,1;0rad)
FEATURE [Part::FeaturePython] CutMaterial  # WARN: FeaturePython — macro-defined, semantics opaque (R4)
  Placement = pos=(-6.4e-14,-157.08,25) rot=(0,0,1;0rad)
